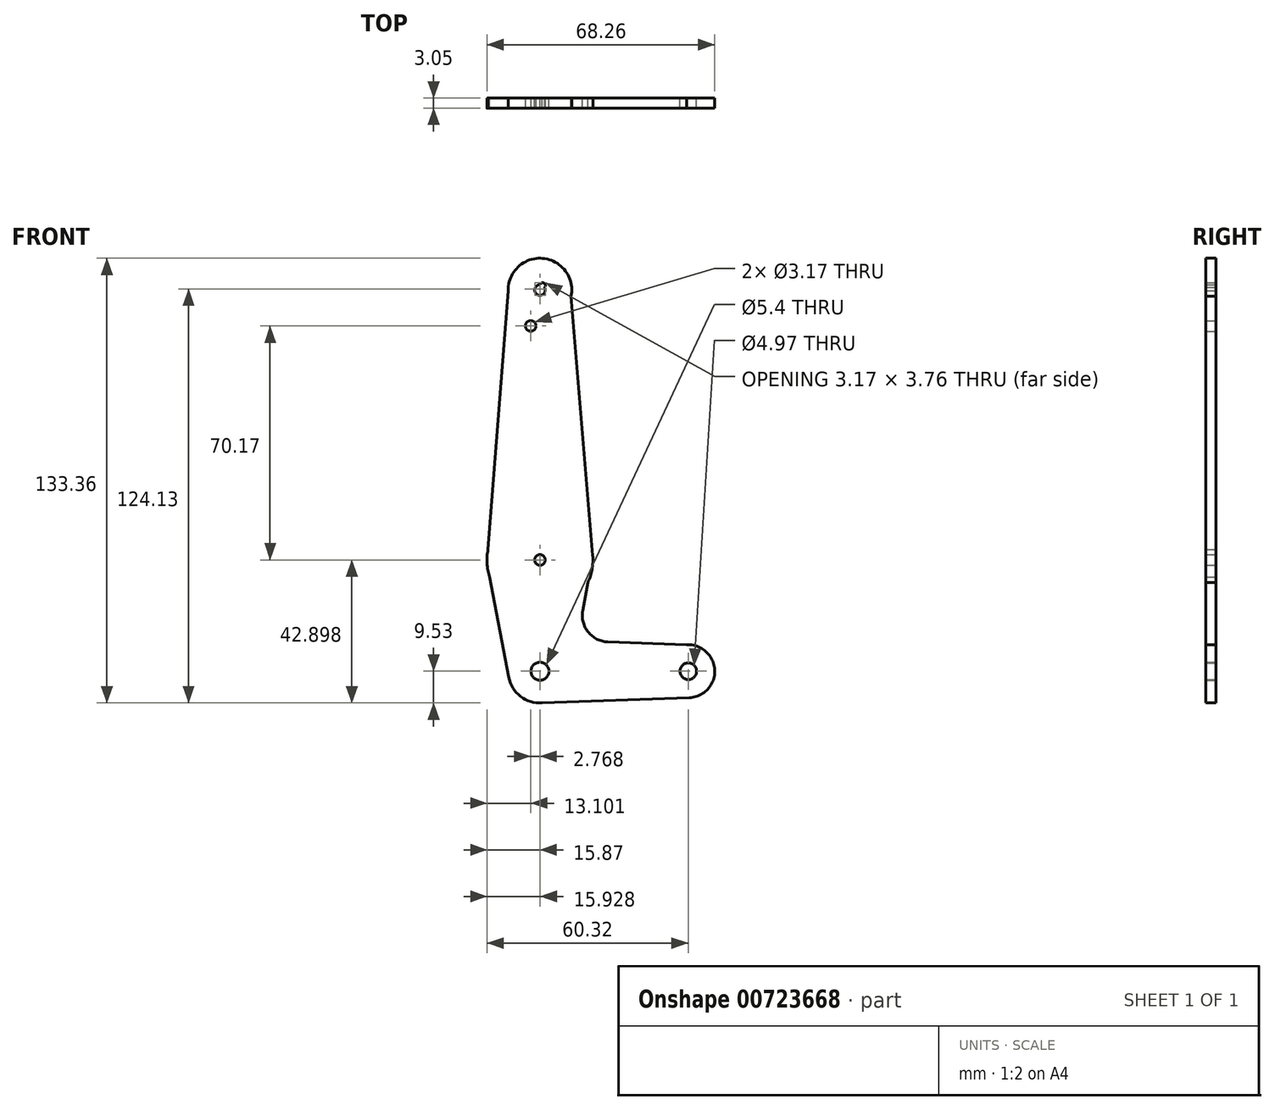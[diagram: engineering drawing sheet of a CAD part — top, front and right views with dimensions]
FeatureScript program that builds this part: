
annotation { "Feature Type Name" : "Feature", "Feature Type Description" : "" }
export const myFeature = defineFeature(function(context is Context, id is Id, definition is map)
    precondition{}
    {
        {
            var Q0;
            Q0=qCreatedBy(makeId("Front.planeOp"),FACE);
            var sketch = newSketch(context, id + "F0", { "sketchPlane" : qUnion([Q0])});
            skLineSegment(sketch, "E0", {"start": v(0, 0) * mm, "end": v(0, 114.3) * mm, "construction": true});
            skLineSegment(sketch, "E1", {"start": v(0, 0) * mm, "end": v(44.45, 0) * mm, "construction": true});
            skCircle(sketch, "E2", {"center": v(0, 114.3) * mm, "radius": 9.53 * mm});
            skCircle(sketch, "E3", {"center": v(0, 0) * mm, "radius": 9.53 * mm});
            skCircle(sketch, "E4", {"center": v(44.45, 0) * mm, "radius": 7.94 * mm});
            skCircle(sketch, "E5", {"center": v(0, 33.37) * mm, "radius": 15.88 * mm});
            skLineSegment(sketch, "E6", {"start": v(-9.52, 114.06) * mm, "end": v(-15.86, 32.62) * mm});
            skLineSegment(sketch, "E7", {"start": v(9.34, 112.42) * mm, "end": v(15.82, 34.69) * mm});
            skLineSegment(sketch, "E8", {"start": v(-15.86, 32.62) * mm, "end": v(-9.36, -1.77) * mm});
            skLineSegment(sketch, "E9", {"start": v(15.82, 34.69) * mm, "end": v(12.82, 18.15) * mm});
            skLineSegment(sketch, "E10", {"start": v(0, -9.53) * mm, "end": v(44.73, -7.93) * mm});
            skCircle(sketch, "E11", {"center": v(0, 114.3) * mm, "radius": 1.59 * mm});
            skCircle(sketch, "E12", {"center": v(0.82, 115.66) * mm, "radius": 0.82 * mm});
            skCircle(sketch, "E13", {"center": v(0, 33.37) * mm, "radius": 1.59 * mm});
            skCircle(sketch, "E14", {"center": v(0, 0) * mm, "radius": 2.7 * mm});
            skCircle(sketch, "E15", {"center": v(44.45, 0) * mm, "radius": 2.49 * mm});
            skLineSegment(sketch, "E16", {"start": v(43.97, 7.92) * mm, "end": v(20.35, 8.79) * mm});
            skCircle(sketch, "E17", {"center": v(-2.77, 103.54) * mm, "radius": 1.59 * mm});
            skPoint(sketch, "E18.newPointA", {"position": v(0, 9.53) * mm});
            skArc(sketch, "E18.filletArc", {"start": v(12.82, 18.15) * mm, "mid": v(14.45, 11.75) * mm, "end": v(20.35, 8.79) * mm});
            skLineSegment(sketch, "E19", {"start": v(9.34, 112.42) * mm, "end": v(16.02, 32.3) * mm});
            skSolve(sketch);
        }
        {
            var Q0;
            Q0 = qSketchRegion(id + "F0", true);
            extrude(context, id + "F1", {"entities" : qUnion([Q0]), "depth" : 3.05 * mm, "offsetDistance" : 25.4 * mm});
        }
    });
